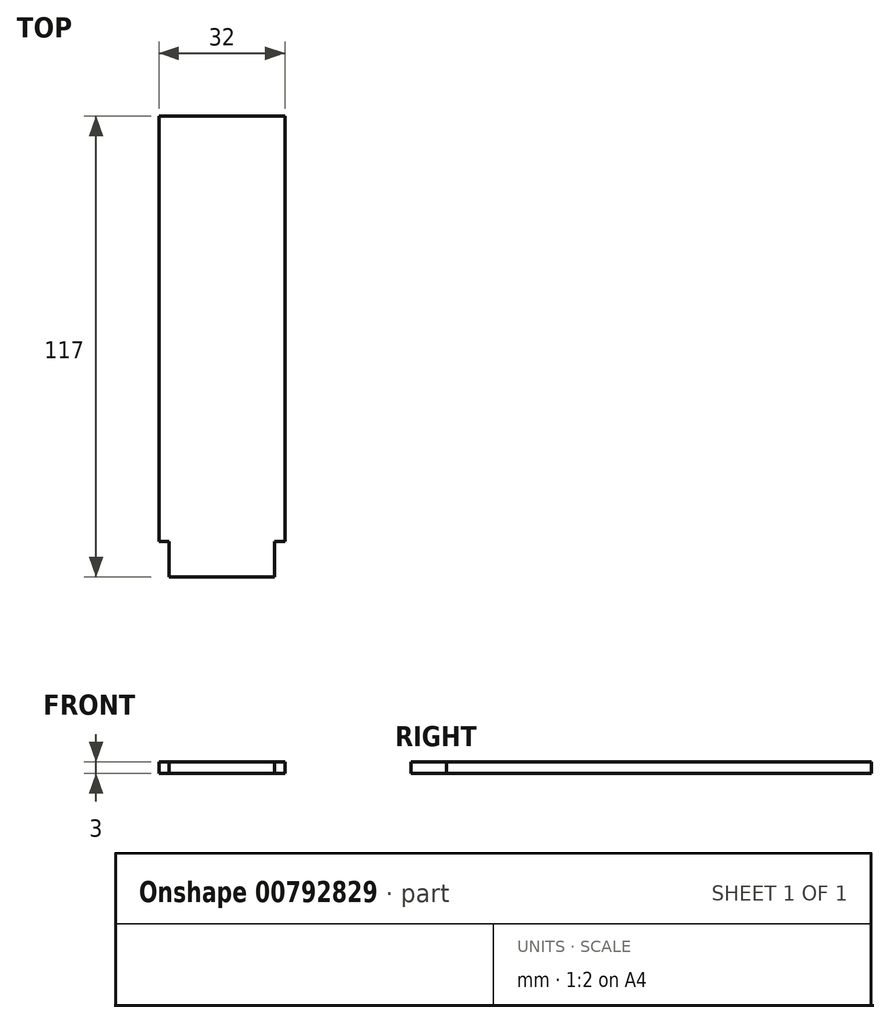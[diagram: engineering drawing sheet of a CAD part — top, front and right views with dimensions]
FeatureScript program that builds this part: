
annotation { "Feature Type Name" : "Feature", "Feature Type Description" : "" }
export const myFeature = defineFeature(function(context is Context, id is Id, definition is map)
    precondition{}
    {
        {
            var Q0;
            Q0=qCreatedBy(makeId("Top.planeOp"),FACE);
            var sketch = newSketch(context, id + "F0", { "sketchPlane" : qUnion([Q0])});
            skLineSegment(sketch, "E0.bottom", {"start": v(16, -56.94) * mm, "end": v(-16, -56.94) * mm});
            skLineSegment(sketch, "E0.top", {"start": v(16, 51.06) * mm, "end": v(-16, 51.06) * mm});
            skLineSegment(sketch, "E0.left", {"start": v(16, -56.94) * mm, "end": v(16, 51.06) * mm});
            skLineSegment(sketch, "E0.right", {"start": v(-16, -56.94) * mm, "end": v(-16, 51.06) * mm});
            skPoint(sketch, "E0.middle", {"position": v(0, -2.94) * mm});
            skSolve(sketch);
        }
        {
            var Q0;
            Q0 = qSketchRegion(id + "F0", true);
            extrude(context, id + "F1", {"entities" : qUnion([Q0]), "depth" : 3 * mm, "offsetDistance" : 25 * mm});
        }
        {
            var Q0;
            Q0=makeQuery(id+"F1.opExtrude","SWEPT_FACE",FACE,{"disambiguationData":[OSD([sQuery(id+"F0.wireOp",EDGE,"E0.bottom")])]});
            var sketch = newSketch(context, id + "F2", { "sketchPlane" : qUnion([Q0])});
            skLineSegment(sketch, "E1", {"start": v(0, 10.1) * mm, "end": v(0, -13.86) * mm, "construction": true});
            skLineSegment(sketch, "E2", {"start": v(0, 3) * mm, "end": v(13.4, 3) * mm});
            skLineSegment(sketch, "E3", {"start": v(13.4, 3) * mm, "end": v(13.4, 0) * mm});
            skLineSegment(sketch, "E4", {"start": v(13.4, 0) * mm, "end": v(0, 0) * mm});
            skLineSegment(sketch, "E5.MirrorCS", {"start": v(0, 3) * mm, "end": v(-13.4, 3) * mm});
            skLineSegment(sketch, "E6.MirrorCS", {"start": v(-13.4, 0) * mm, "end": v(0, 0) * mm});
            skLineSegment(sketch, "E7.MirrorCS", {"start": v(-13.4, 3) * mm, "end": v(-13.4, 0) * mm});
            skSolve(sketch);
        }
        {
            var Q0;
            Q0 = qSketchRegion(id + "F2", true);
            extrude(context, id + "F3", {"entities" : qUnion([Q0]), "operationType" : NewBodyOperationType.ADD, "depth" : 9 * mm, "offsetDistance" : 25 * mm});
        }
    });
